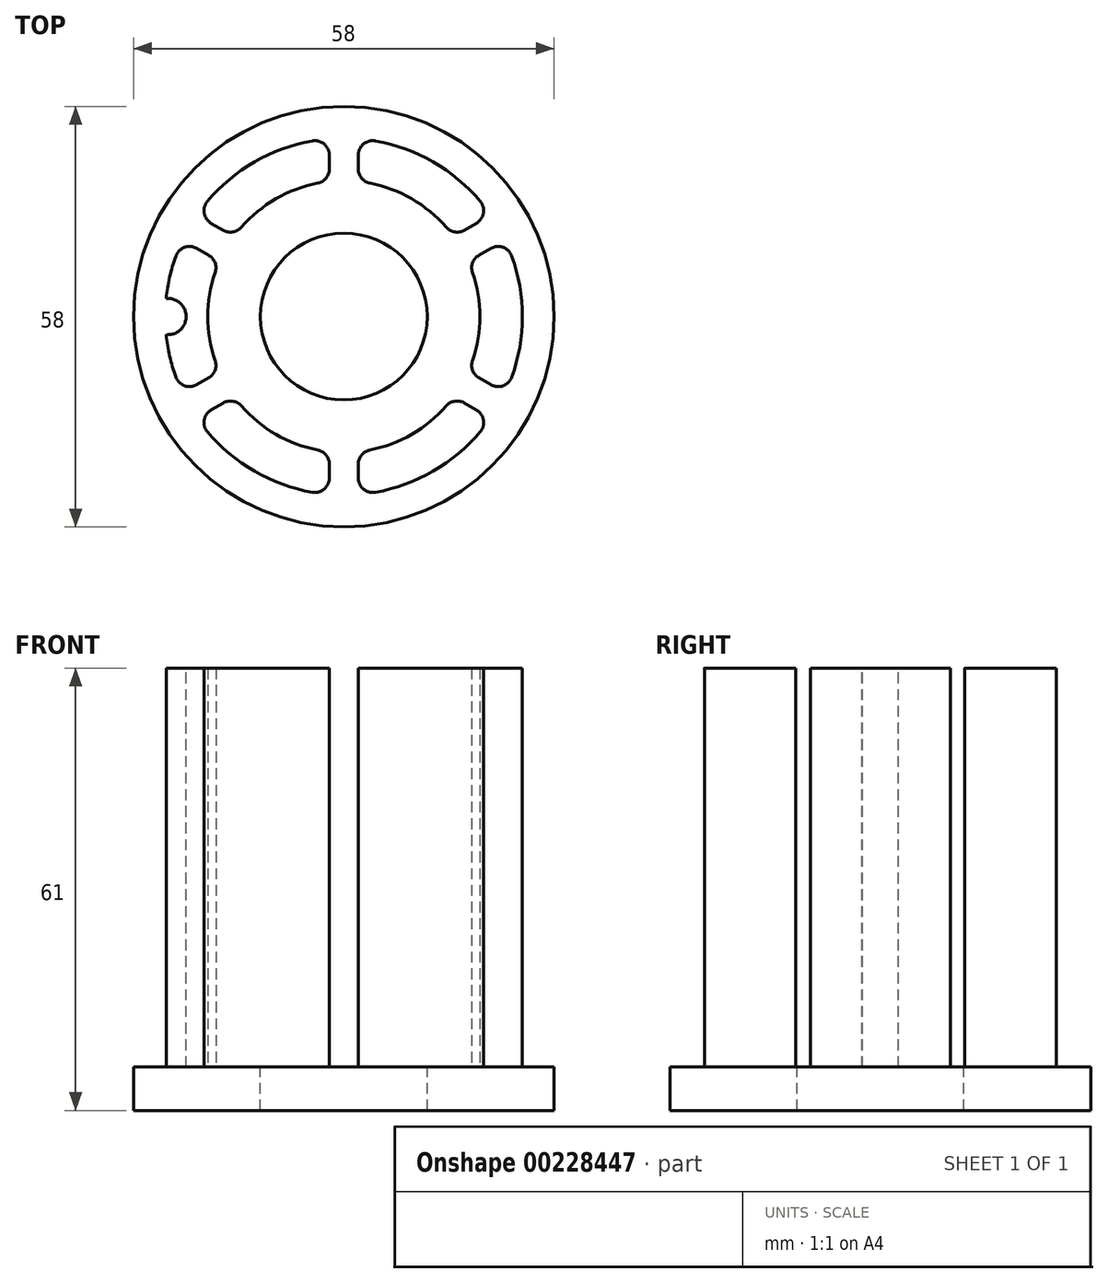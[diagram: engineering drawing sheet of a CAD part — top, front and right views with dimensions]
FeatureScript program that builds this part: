
annotation { "Feature Type Name" : "Feature", "Feature Type Description" : "" }
export const myFeature = defineFeature(function(context is Context, id is Id, definition is map)
    precondition{}
    {
        {
            var Q0;
            Q0=qCreatedBy(makeId("Top.planeOp"),FACE);
            var sketch = newSketch(context, id + "F0", { "sketchPlane" : qUnion([Q0])});
            skArc(sketch, "E0", {"start": v(3.61, -18.4) * mm, "mid": v(9.38, -16.24) * mm, "end": v(14.13, -12.33) * mm});
            skArc(sketch, "E1", {"start": v(4.35, -24.24) * mm, "mid": v(12.31, -21.33) * mm, "end": v(18.81, -15.89) * mm});
            skLineSegment(sketch, "E2", {"start": v(0, 0) * mm, "end": v(0, -24.63) * mm, "construction": true});
            skLineSegment(sketch, "E3.0", {"start": v(-2, -20.36) * mm, "end": v(-2, -22.27) * mm});
            skLineSegment(sketch, "E4.0", {"start": v(2, -20.36) * mm, "end": v(2, -22.27) * mm});
            skLineSegment(sketch, "E5.1.0", {"start": v(16.63, -11.91) * mm, "end": v(18.29, -12.87) * mm});
            skLineSegment(sketch, "E5.1.1", {"start": v(18.63, -8.45) * mm, "end": v(20.29, -9.4) * mm});
            skLineSegment(sketch, "E5.2.0", {"start": v(18.63, 8.45) * mm, "end": v(20.29, 9.4) * mm});
            skLineSegment(sketch, "E5.2.1", {"start": v(16.63, 11.91) * mm, "end": v(18.29, 12.87) * mm});
            skLineSegment(sketch, "E5.3.0", {"start": v(2, 20.36) * mm, "end": v(2, 22.27) * mm});
            skLineSegment(sketch, "E5.3.1", {"start": v(-2, 20.36) * mm, "end": v(-2, 22.27) * mm});
            skLineSegment(sketch, "E5.4.0", {"start": v(-16.63, 11.91) * mm, "end": v(-18.29, 12.87) * mm});
            skLineSegment(sketch, "E5.4.1", {"start": v(-18.63, 8.45) * mm, "end": v(-20.29, 9.4) * mm});
            skLineSegment(sketch, "E5.5.0", {"start": v(-18.63, -8.45) * mm, "end": v(-20.29, -9.4) * mm});
            skLineSegment(sketch, "E5.5.1", {"start": v(-16.63, -11.91) * mm, "end": v(-18.29, -12.87) * mm});
            skArc(sketch, "E6.trimOffspring", {"start": v(-18.81, -15.89) * mm, "mid": v(-12.31, -21.33) * mm, "end": v(-4.35, -24.24) * mm});
            skArc(sketch, "E7.trimOffspring", {"start": v(-14.13, -12.33) * mm, "mid": v(-9.37, -16.24) * mm, "end": v(-3.61, -18.4) * mm});
            skArc(sketch, "E8.trimOffspring", {"start": v(-23.17, 8.35) * mm, "mid": v(-24.63, 0) * mm, "end": v(-23.17, -8.35) * mm});
            skArc(sketch, "E9.trimOffspring", {"start": v(-17.74, 6.07) * mm, "mid": v(-18.75, 0) * mm, "end": v(-17.74, -6.07) * mm});
            skArc(sketch, "E10.trimOffspring", {"start": v(23.17, -8.35) * mm, "mid": v(24.63, 0) * mm, "end": v(23.17, 8.35) * mm});
            skArc(sketch, "E11.trimOffspring", {"start": v(17.74, -6.07) * mm, "mid": v(18.75, 0) * mm, "end": v(17.74, 6.07) * mm});
            skArc(sketch, "E12.trimOffspring", {"start": v(14.13, 12.33) * mm, "mid": v(9.38, 16.24) * mm, "end": v(3.61, 18.4) * mm});
            skArc(sketch, "E13.trimOffspring", {"start": v(18.81, 15.89) * mm, "mid": v(12.31, 21.33) * mm, "end": v(4.35, 24.24) * mm});
            skArc(sketch, "E14.trimOffspring", {"start": v(-3.61, 18.4) * mm, "mid": v(-9.37, 16.24) * mm, "end": v(-14.13, 12.33) * mm});
            skArc(sketch, "E15.trimOffspring", {"start": v(-4.35, 24.24) * mm, "mid": v(-12.31, 21.33) * mm, "end": v(-18.81, 15.89) * mm});
            skPoint(sketch, "E16.newPointA", {"position": v(-22.33, 10.58) * mm});
            skArc(sketch, "E16.filletArc", {"start": v(-20.29, 9.4) * mm, "mid": v(-21.97, 9.55) * mm, "end": v(-23.17, 8.35) * mm});
            skPoint(sketch, "E17.newPointB", {"position": v(-22.33, -10.58) * mm});
            skArc(sketch, "E17.filletArc", {"start": v(-23.17, -8.35) * mm, "mid": v(-21.97, -9.55) * mm, "end": v(-20.29, -9.4) * mm});
            skPoint(sketch, "E18.newPointB", {"position": v(-20.33, -14.04) * mm});
            skArc(sketch, "E18.filletArc", {"start": v(-18.29, -12.87) * mm, "mid": v(-19.26, -14.25) * mm, "end": v(-18.81, -15.89) * mm});
            skPoint(sketch, "E19.newPointB", {"position": v(-2, -24.63) * mm});
            skArc(sketch, "E19.filletArc", {"start": v(-4.35, -24.24) * mm, "mid": v(-2.72, -23.8) * mm, "end": v(-2, -22.27) * mm});
            skPoint(sketch, "E20.newPointA", {"position": v(2, -24.63) * mm});
            skArc(sketch, "E20.filletArc", {"start": v(2, -22.27) * mm, "mid": v(2.72, -23.8) * mm, "end": v(4.35, -24.24) * mm});
            skPoint(sketch, "E21.visualSharp", {"position": v(-2, -18.64) * mm});
            skArc(sketch, "E21.filletArc", {"start": v(-2, -20.36) * mm, "mid": v(-2.46, -19.1) * mm, "end": v(-3.61, -18.4) * mm});
            skPoint(sketch, "E22.visualSharp", {"position": v(-15.15, -11.05) * mm});
            skArc(sketch, "E22.filletArc", {"start": v(-14.13, -12.33) * mm, "mid": v(-15.3, -11.67) * mm, "end": v(-16.63, -11.91) * mm});
            skPoint(sketch, "E23.visualSharp", {"position": v(-17.15, -7.59) * mm});
            skArc(sketch, "E23.filletArc", {"start": v(-18.63, -8.45) * mm, "mid": v(-17.76, -7.42) * mm, "end": v(-17.74, -6.07) * mm});
            skPoint(sketch, "E24.visualSharp", {"position": v(-17.15, 7.59) * mm});
            skArc(sketch, "E24.filletArc", {"start": v(-17.74, 6.07) * mm, "mid": v(-17.76, 7.42) * mm, "end": v(-18.63, 8.45) * mm});
            skPoint(sketch, "E25.newPointA", {"position": v(-20.33, 14.04) * mm});
            skArc(sketch, "E25.filletArc", {"start": v(-18.81, 15.89) * mm, "mid": v(-19.26, 14.25) * mm, "end": v(-18.29, 12.87) * mm});
            skPoint(sketch, "E26.visualSharp", {"position": v(-15.15, 11.05) * mm});
            skArc(sketch, "E26.filletArc", {"start": v(-16.63, 11.91) * mm, "mid": v(-15.3, 11.67) * mm, "end": v(-14.13, 12.33) * mm});
            skPoint(sketch, "E27.visualSharp", {"position": v(2, -18.64) * mm});
            skArc(sketch, "E27.filletArc", {"start": v(3.61, -18.4) * mm, "mid": v(2.46, -19.1) * mm, "end": v(2, -20.36) * mm});
            skPoint(sketch, "E28.visualSharp", {"position": v(15.15, -11.05) * mm});
            skArc(sketch, "E28.filletArc", {"start": v(16.63, -11.91) * mm, "mid": v(15.3, -11.67) * mm, "end": v(14.13, -12.33) * mm});
            skPoint(sketch, "E29.newPointA", {"position": v(20.33, -14.04) * mm});
            skArc(sketch, "E29.filletArc", {"start": v(18.81, -15.89) * mm, "mid": v(19.26, -14.25) * mm, "end": v(18.29, -12.87) * mm});
            skPoint(sketch, "E30.visualSharp", {"position": v(-2, 18.64) * mm});
            skArc(sketch, "E30.filletArc", {"start": v(-3.61, 18.4) * mm, "mid": v(-2.46, 19.1) * mm, "end": v(-2, 20.36) * mm});
            skPoint(sketch, "E31.newPointA", {"position": v(-2, 24.63) * mm});
            skArc(sketch, "E31.filletArc", {"start": v(-2, 22.27) * mm, "mid": v(-2.72, 23.8) * mm, "end": v(-4.35, 24.24) * mm});
            skPoint(sketch, "E32.visualSharp", {"position": v(2, 18.64) * mm});
            skArc(sketch, "E32.filletArc", {"start": v(2, 20.36) * mm, "mid": v(2.46, 19.1) * mm, "end": v(3.61, 18.4) * mm});
            skPoint(sketch, "E33.newPointA", {"position": v(2, 24.63) * mm});
            skArc(sketch, "E33.filletArc", {"start": v(4.35, 24.24) * mm, "mid": v(2.72, 23.8) * mm, "end": v(2, 22.27) * mm});
            skPoint(sketch, "E34.visualSharp", {"position": v(15.15, 11.05) * mm});
            skArc(sketch, "E34.filletArc", {"start": v(14.13, 12.33) * mm, "mid": v(15.3, 11.67) * mm, "end": v(16.63, 11.91) * mm});
            skPoint(sketch, "E35.newPointA", {"position": v(20.33, 14.04) * mm});
            skArc(sketch, "E35.filletArc", {"start": v(18.29, 12.87) * mm, "mid": v(19.26, 14.25) * mm, "end": v(18.81, 15.89) * mm});
            skPoint(sketch, "E36.visualSharp", {"position": v(17.15, 7.59) * mm});
            skArc(sketch, "E36.filletArc", {"start": v(18.63, 8.45) * mm, "mid": v(17.76, 7.42) * mm, "end": v(17.74, 6.07) * mm});
            skPoint(sketch, "E37.newPointA", {"position": v(22.33, 10.58) * mm});
            skArc(sketch, "E37.filletArc", {"start": v(23.17, 8.35) * mm, "mid": v(21.97, 9.55) * mm, "end": v(20.29, 9.4) * mm});
            skPoint(sketch, "E38.visualSharp", {"position": v(17.15, -7.59) * mm});
            skArc(sketch, "E38.filletArc", {"start": v(17.74, -6.07) * mm, "mid": v(17.76, -7.42) * mm, "end": v(18.63, -8.45) * mm});
            skPoint(sketch, "E39.newPointA", {"position": v(22.33, -10.58) * mm});
            skArc(sketch, "E39.filletArc", {"start": v(20.29, -9.4) * mm, "mid": v(21.97, -9.55) * mm, "end": v(23.17, -8.35) * mm});
            skSolve(sketch);
        }
        {
            var Q0;
            Q0=makeQuery(id+"F0.imprint","IMPRINT",FACE,{"disambiguationData":[TD([[makeQuery(id+"F0.imprint","IMPRINT",EDGE,{"derivedFrom":sQuery(id+"F0.wireOp",EDGE,"E3.0")}),-1.0]])]});
            var Q1;
            Q1=makeQuery(id+"F0.imprint","IMPRINT",FACE,{"disambiguationData":[TD([[makeQuery(id+"F0.imprint","IMPRINT",EDGE,{"derivedFrom":sQuery(id+"F0.wireOp",EDGE,"E0")}),-1.0]])]});
            var Q2;
            Q2=makeQuery(id+"F0.imprint","IMPRINT",FACE,{"disambiguationData":[TD([[makeQuery(id+"F0.imprint","IMPRINT",EDGE,{"derivedFrom":sQuery(id+"F0.wireOp",EDGE,"E5.1.1")}),1.0]])]});
            var Q3;
            Q3=makeQuery(id+"F0.imprint","IMPRINT",FACE,{"disambiguationData":[TD([[makeQuery(id+"F0.imprint","IMPRINT",EDGE,{"derivedFrom":sQuery(id+"F0.wireOp",EDGE,"E5.4.1")}),1.0]])]});
            var Q4;
            Q4=makeQuery(id+"F0.imprint","IMPRINT",FACE,{"disambiguationData":[TD([[makeQuery(id+"F0.imprint","IMPRINT",EDGE,{"derivedFrom":sQuery(id+"F0.wireOp",EDGE,"E5.3.1")}),1.0]])]});
            var Q5;
            Q5=makeQuery(id+"F0.imprint","IMPRINT",FACE,{"disambiguationData":[TD([[makeQuery(id+"F0.imprint","IMPRINT",EDGE,{"derivedFrom":sQuery(id+"F0.wireOp",EDGE,"E5.2.1")}),1.0]])]});
            extrude(context, id + "F1", {"entities" : qUnion([Q0, Q1, Q2, Q3, Q4, Q5]), "depth" : 55 * mm});
        }
        {
            var Q0;
            Q0=qCreatedBy(makeId("Top.planeOp"),FACE);
            var sketch = newSketch(context, id + "F2", { "sketchPlane" : qUnion([Q0])});
            skCircle(sketch, "E40", {"center": v(0, 0) * mm, "radius": 29 * mm});
            skCircle(sketch, "E41", {"center": v(0, 0) * mm, "radius": 11.5 * mm});
            skSolve(sketch);
        }
        {
            var Q0;
            Q0=makeQuery(id+"F2.imprint","IMPRINT",FACE,{"disambiguationData":[TD([[makeQuery(id+"F2.imprint","IMPRINT",EDGE,{"derivedFrom":sQuery(id+"F2.wireOp",EDGE,"E40")}),1.0]])]});
            extrude(context, id + "F3", {"entities" : qUnion([Q0]), "oppositeDirection" : true, "depth" : 6 * mm});
        }
        {
            var Q0;
            Q0=makeQuery(id+"F1.opExtrude","CAP_FACE",FACE,{"disambiguationData":[OSD([sQuery(id+"F0.wireOp",EDGE,"E5.2.1"),sQuery(id+"F0.wireOp",EDGE,"E5.3.0"),sQuery(id+"F0.wireOp",EDGE,"E12.trimOffspring"),sQuery(id+"F0.wireOp",EDGE,"E13.trimOffspring"),sQuery(id+"F0.wireOp",EDGE,"E32.filletArc"),sQuery(id+"F0.wireOp",EDGE,"E33.filletArc"),sQuery(id+"F0.wireOp",EDGE,"E34.filletArc"),sQuery(id+"F0.wireOp",EDGE,"E35.filletArc")])],"isStart":false});
            cPlane(context, id + "F4", {"entities" : qUnion([Q0]), "cplaneType" : CPlaneType.OFFSET, "offset" : 25 * mm, "width" : 150 * mm, "height" : 150 * mm});
        }
        {
            var Q0;
            Q0=qCreatedBy(id+"F4.planeOp",FACE);
            var sketch = newSketch(context, id + "F5", { "sketchPlane" : qUnion([Q0])});
            skLineSegment(sketch, "E42", {"start": v(0, 0) * mm, "end": v(24.25, 0) * mm, "construction": true});
            skCircle(sketch, "E43", {"center": v(24.25, 0) * mm, "radius": 2.5 * mm});
            skSolve(sketch);
        }
        {
            var Q0;
            Q0=qCreatedBy(makeId("Right.planeOp"),FACE);
            var sketch = newSketch(context, id + "F6", { "sketchPlane" : qUnion([Q0])});
            skLineSegment(sketch, "E44", {"start": v(0, 0) * mm, "end": v(0, 121.43) * mm, "construction": true});
            skSolve(sketch);
        }
        {
            var Q0;
            Q0=makeQuery(id+"F5.imprint","IMPRINT",FACE,{"disambiguationData":[TD([[makeQuery(id+"F5.imprint","IMPRINT",EDGE,{"derivedFrom":sQuery(id+"F5.wireOp",EDGE,"E43")}),1.0]])]});
            extrude(context, id + "F7", {"entities" : qUnion([Q0]), "oppositeDirection" : true, "depth" : 100 * mm});
        }
        {
            var Q0;
            Q0=makeQuery(id+"F7.opExtrude","SWEPT_BODY",BODY,{"disambiguationData":[OSD([sQuery(id+"F5.wireOp",EDGE,"E43")])]});
            var Q1;
            Q1=sQuery(id+"F6.wireOp",EDGE,"E44");
            circularPattern(context, id + "F8", {"entities" : qUnion([Q0]), "axis" : qUnion([Q1]), "angle" : 360 * degree, "instanceCount" : 6, "equalSpace" : true});
        }
        {
            var Q0;
            Q0=makeQuery(id+"F7.opExtrude","SWEPT_BODY",BODY,{"disambiguationData":[OSD([sQuery(id+"F5.wireOp",EDGE,"E43")])]});
            var Q1;
            Q1=makeQuery(id+"F8.opPattern","COPY",BODY,{"derivedFrom":makeQuery(id+"F7.opExtrude","SWEPT_BODY",BODY,{"disambiguationData":[OSD([sQuery(id+"F5.wireOp",EDGE,"E43")])]}),"instanceName":"2"});
            var Q2;
            Q2=makeQuery(id+"F8.opPattern","COPY",BODY,{"derivedFrom":makeQuery(id+"F7.opExtrude","SWEPT_BODY",BODY,{"disambiguationData":[OSD([sQuery(id+"F5.wireOp",EDGE,"E43")])]}),"instanceName":"3"});
            var Q3;
            Q3=makeQuery(id+"F8.opPattern","COPY",BODY,{"derivedFrom":makeQuery(id+"F7.opExtrude","SWEPT_BODY",BODY,{"disambiguationData":[OSD([sQuery(id+"F5.wireOp",EDGE,"E43")])]}),"instanceName":"4"});
            var Q4;
            Q4=makeQuery(id+"F8.opPattern","COPY",BODY,{"derivedFrom":makeQuery(id+"F7.opExtrude","SWEPT_BODY",BODY,{"disambiguationData":[OSD([sQuery(id+"F5.wireOp",EDGE,"E43")])]}),"instanceName":"5"});
            var Q5;
            Q5=makeQuery(id+"F8.opPattern","COPY",BODY,{"derivedFrom":makeQuery(id+"F7.opExtrude","SWEPT_BODY",BODY,{"disambiguationData":[OSD([sQuery(id+"F5.wireOp",EDGE,"E43")])]}),"instanceName":"1"});
            var Q6;
            Q6=makeQuery(id+"F1.opExtrude","SWEPT_BODY",BODY,{"disambiguationData":[OSD([sQuery(id+"F0.wireOp",EDGE,"E5.4.1"),sQuery(id+"F0.wireOp",EDGE,"E5.5.0"),sQuery(id+"F0.wireOp",EDGE,"E8.trimOffspring"),sQuery(id+"F0.wireOp",EDGE,"E9.trimOffspring"),sQuery(id+"F0.wireOp",EDGE,"E16.filletArc"),sQuery(id+"F0.wireOp",EDGE,"E17.filletArc"),sQuery(id+"F0.wireOp",EDGE,"E23.filletArc"),sQuery(id+"F0.wireOp",EDGE,"E24.filletArc")])]});
            booleanBodies(context, id + "F9", {"operationType" : BooleanOperationType.SUBTRACTION, "tools" : qUnion([Q0, Q1, Q2, Q3, Q4, Q5]), "targets" : qUnion([Q6])});
        }
    });
